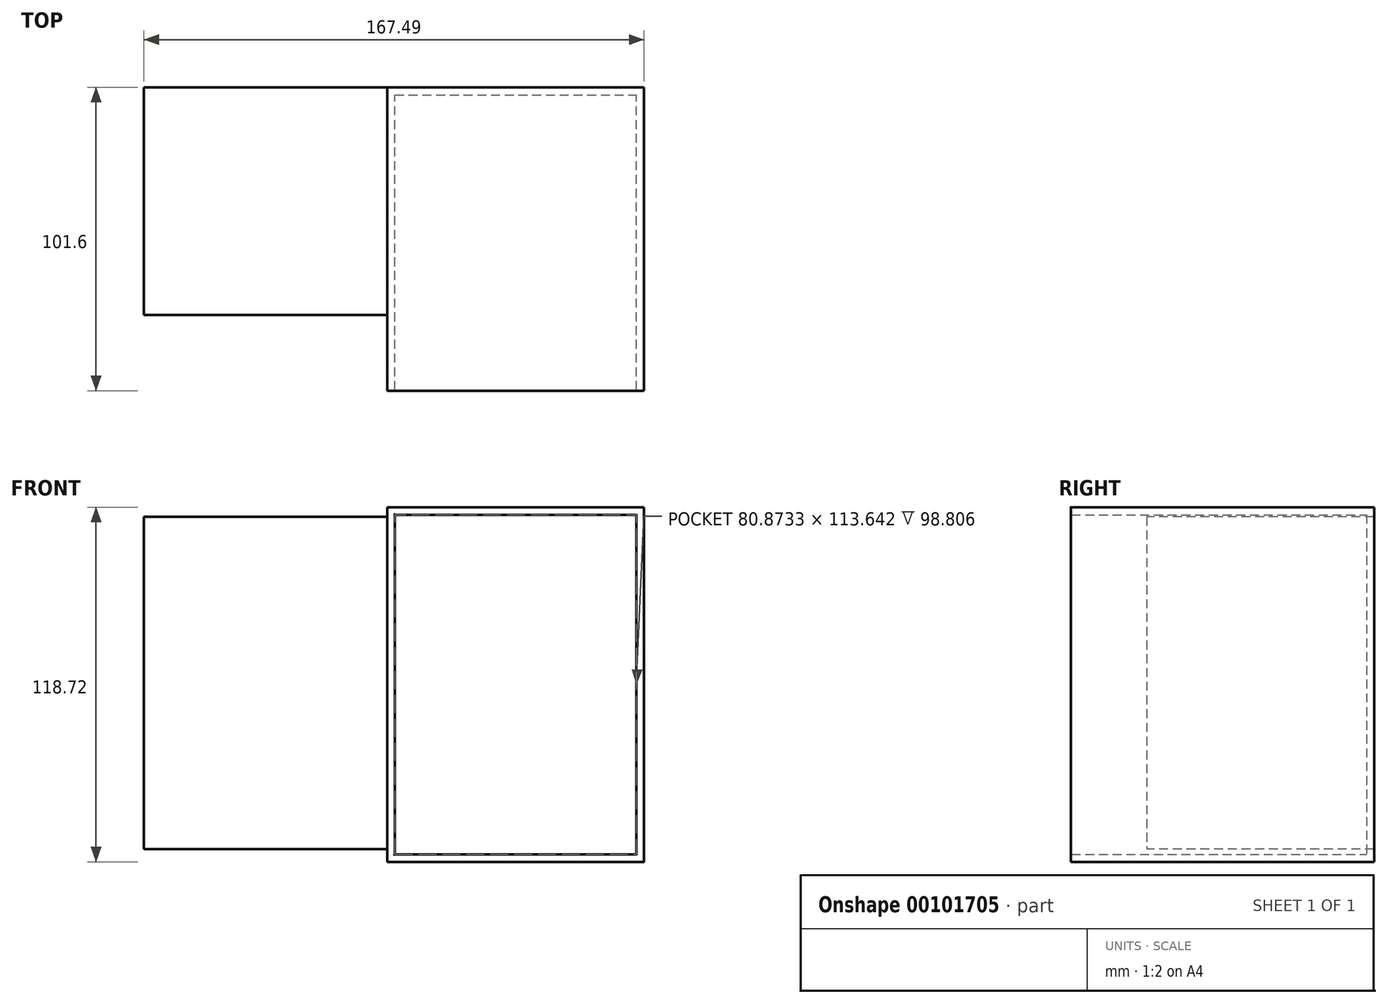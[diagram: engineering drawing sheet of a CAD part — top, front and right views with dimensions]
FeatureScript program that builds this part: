
annotation { "Feature Type Name" : "Feature", "Feature Type Description" : "" }
export const myFeature = defineFeature(function(context is Context, id is Id, definition is map)
    precondition{}
    {
        {
            var Q0;
            Q0=qCreatedBy(makeId("Front.planeOp"),FACE);
            var sketch = newSketch(context, id + "F0", { "sketchPlane" : qUnion([Q0])});
            skLineSegment(sketch, "E0.bottom", {"start": v(-37.48, 59.76) * mm, "end": v(48.47, 59.76) * mm});
            skLineSegment(sketch, "E0.top", {"start": v(-37.48, -58.96) * mm, "end": v(48.47, -58.96) * mm});
            skLineSegment(sketch, "E0.left", {"start": v(-37.48, 59.76) * mm, "end": v(-37.48, -58.96) * mm});
            skLineSegment(sketch, "E0.right", {"start": v(48.47, 59.76) * mm, "end": v(48.47, -58.96) * mm});
            skSolve(sketch);
        }
        {
            var Q0;
            Q0=makeQuery(id+"F0.imprint","IMPRINT",FACE,{"disambiguationData":[TD([[makeQuery(id+"F0.imprint","IMPRINT",EDGE,{"derivedFrom":sQuery(id+"F0.wireOp",EDGE,"E0.bottom")}),-1.0]])]});
            extrude(context, id + "F1", {"entities" : qUnion([Q0]), "depth" : 101.6 * mm});
        }
        {
            var Q0;
            Q0=makeQuery(id+"F1.opExtrude","CAP_FACE",FACE,{"disambiguationData":[OSD([sQuery(id+"F0.wireOp",EDGE,"E0.bottom"),sQuery(id+"F0.wireOp",EDGE,"E0.top"),sQuery(id+"F0.wireOp",EDGE,"E0.left"),sQuery(id+"F0.wireOp",EDGE,"E0.right")])],"isStart":false});
            shell(context, id + "F3", {"entities" : qUnion([Q0]), "thickness" : 2.54 * mm});
        }
        {
            var Q0;
            Q0=makeQuery(id+"F1.opExtrude","CAP_EDGE",EDGE,{"disambiguationData":[OSD([sQuery(id+"F0.wireOp",EDGE,"E0.right")])],"isStart":false});
            var Q1;
            {var subQ0=sQuery(id+"F0.wireOp",EDGE,"E0.bottom");Q1=makeQuery(id+"F3.opShell","OFFSET_EDGE",EDGE,{"disambiguationData":[OSD([subQ0]),TDD([makeQuery(id+"F1.opExtrude","CAP_EDGE",EDGE,{"disambiguationData":[OSD([subQ0])],"isStart":false})])]});}
            var Q2;
            {var subQ0=sQuery(id+"F0.wireOp",EDGE,"E0.left");Q2=makeQuery(id+"F3.opShell","OFFSET_EDGE",EDGE,{"disambiguationData":[OSD([subQ0]),TDD([makeQuery(id+"F1.opExtrude","CAP_EDGE",EDGE,{"disambiguationData":[OSD([subQ0])],"isStart":false})])]});}
            var Q3;
            {var subQ0=sQuery(id+"F0.wireOp",EDGE,"E0.top");Q3=makeQuery(id+"F3.opShell","OFFSET_EDGE",EDGE,{"disambiguationData":[OSD([subQ0]),TDD([makeQuery(id+"F1.opExtrude","CAP_EDGE",EDGE,{"disambiguationData":[OSD([subQ0])],"isStart":false})])]});}
            fillet(context, id + "F4", {"entities" : qUnion([Q0, Q1, Q2, Q3]), "radius" : 0.25 * mm, "tangentPropagation" : true, "allowEdgeOverflow" : false});
        }
        {
            var Q0;
            Q0=qCreatedBy(makeId("Front.planeOp"),FACE);
            var sketch = newSketch(context, id + "F2", { "sketchPlane" : qUnion([Q0])});
            skLineSegment(sketch, "E1.bottom", {"start": v(-119.02, 56.54) * mm, "end": v(-37.35, 56.54) * mm});
            skLineSegment(sketch, "E1.top", {"start": v(-119.02, -54.65) * mm, "end": v(-37.35, -54.65) * mm});
            skLineSegment(sketch, "E1.left", {"start": v(-119.02, 56.54) * mm, "end": v(-119.02, -54.65) * mm});
            skLineSegment(sketch, "E1.right", {"start": v(-37.35, 56.54) * mm, "end": v(-37.35, -54.65) * mm});
            skSolve(sketch);
        }
        {
            var Q0;
            Q0=makeQuery(id+"F2.imprint","IMPRINT",FACE,{"disambiguationData":[TD([[makeQuery(id+"F2.imprint","IMPRINT",EDGE,{"derivedFrom":sQuery(id+"F2.wireOp",EDGE,"E1.bottom")}),-1.0]])]});
            extrude(context, id + "F5", {"entities" : qUnion([Q0]), "operationType" : NewBodyOperationType.ADD, "depth" : 76.2 * mm});
        }
    });
